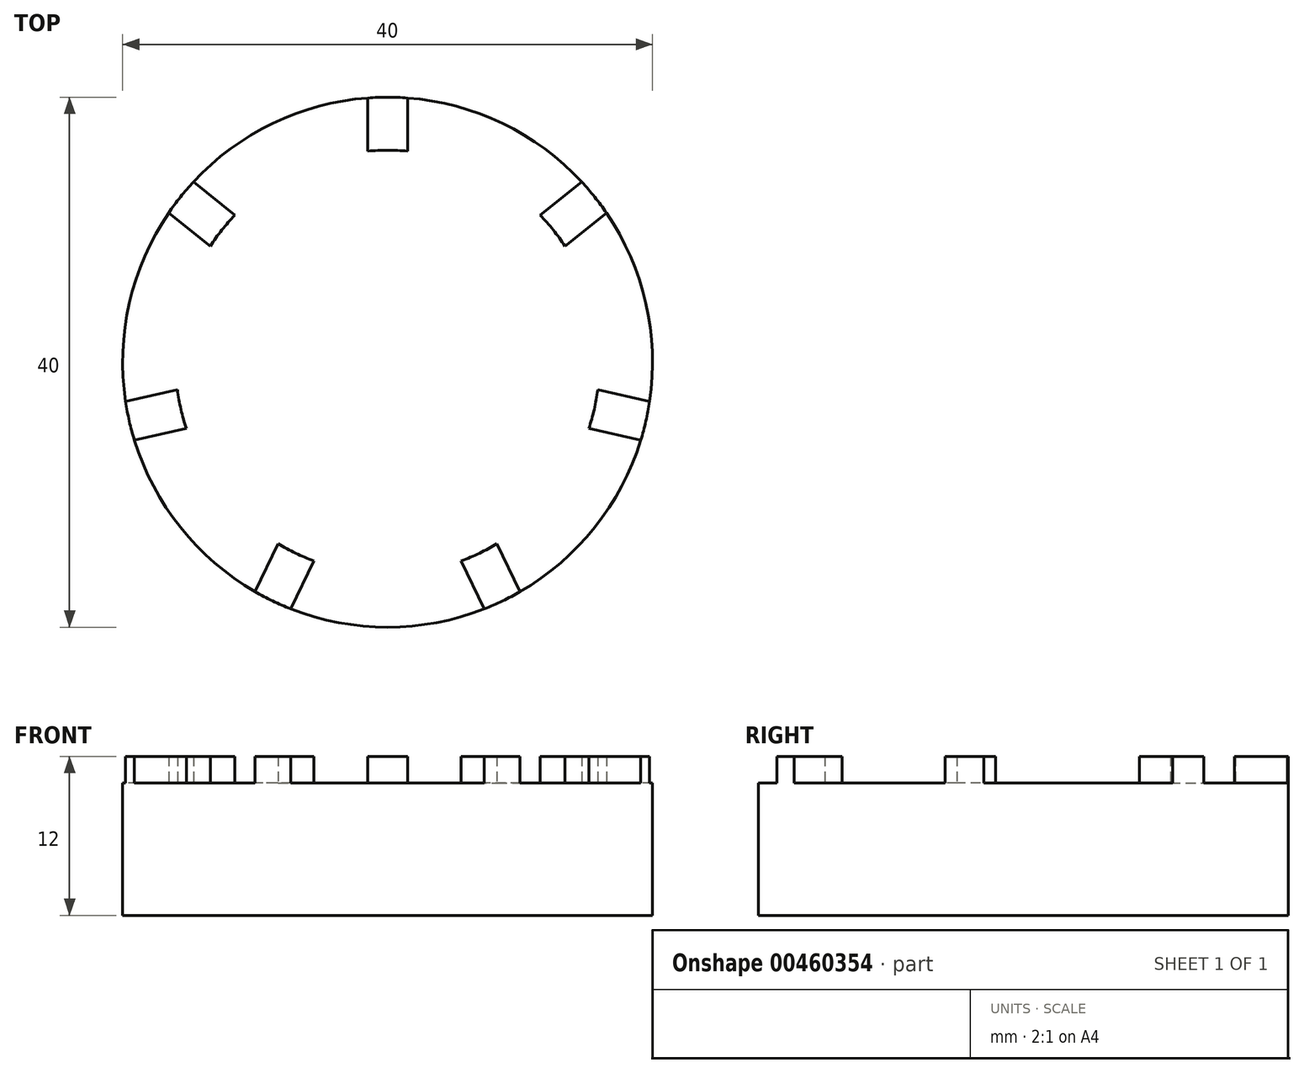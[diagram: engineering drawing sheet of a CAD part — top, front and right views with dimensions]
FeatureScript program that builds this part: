
annotation { "Feature Type Name" : "Feature", "Feature Type Description" : "" }
export const myFeature = defineFeature(function(context is Context, id is Id, definition is map)
    precondition{}
    {
        {
            var Q0;
            Q0=qCreatedBy(makeId("Top.planeOp"),FACE);
            var sketch = newSketch(context, id + "F0", { "sketchPlane" : qUnion([Q0])});
            skCircle(sketch, "E0", {"center": v(0, 0) * mm, "radius": 20 * mm});
            skSolve(sketch);
        }
        {
            var Q0;
            Q0=makeQuery(id+"F0.imprint","IMPRINT",FACE,{"disambiguationData":[TD([[makeQuery(id+"F0.imprint","IMPRINT",EDGE,{"derivedFrom":sQuery(id+"F0.wireOp",EDGE,"E0")}),1.0]])]});
            extrude(context, id + "F1", {"entities" : qUnion([Q0]), "depth" : 10 * mm});
        }
        {
            var Q0;
            Q0=makeQuery(id+"F1.opExtrude","CAP_FACE",FACE,{"disambiguationData":[OSD([sQuery(id+"F0.wireOp",EDGE,"E0")])],"isStart":false});
            var sketch = newSketch(context, id + "F2", { "sketchPlane" : qUnion([Q0])});
            skArc(sketch, "E1.0", {"start": v(1.5, 19.94) * mm, "mid": v(0, 20) * mm, "end": v(-1.5, 19.94) * mm});
            skArc(sketch, "E2", {"start": v(1.5, 15.93) * mm, "mid": v(0, 16) * mm, "end": v(-1.5, 15.93) * mm});
            skLineSegment(sketch, "E3", {"start": v(-1.5, 15.93) * mm, "end": v(-1.5, 19.94) * mm});
            skLineSegment(sketch, "E4", {"start": v(1.5, 15.93) * mm, "end": v(1.5, 19.94) * mm});
            skLineSegment(sketch, "E5", {"start": v(0, 0) * mm, "end": v(0, 16) * mm, "construction": true});
            skSolve(sketch);
        }
        {
            var Q0;
            Q0 = qSketchRegion(id + "F2", true);
            extrude(context, id + "F3", {"entities" : qUnion([Q0]), "operationType" : NewBodyOperationType.ADD, "depth" : 2 * mm});
        }
        {
            var Q0;
            Q0=makeQuery(id+"F1.opExtrude","SWEPT_BODY",BODY,{"disambiguationData":[OSD([sQuery(id+"F0.wireOp",EDGE,"E0")])]});
            var Q1;
            Q1=makeQuery(id+"F3.boolean.opBoolean","MERGE",FACE,{"derivedFrom":[makeQuery(id+"F1.opExtrude","SWEPT_FACE",FACE,{"disambiguationData":[OSD([sQuery(id+"F0.wireOp",EDGE,"E0")])]}),makeQuery(id+"F3.opExtrude","SWEPT_FACE",FACE,{"disambiguationData":[OSD([sQuery(id+"F2.wireOp",EDGE,"E1.0")])]})]});
            circularPattern(context, id + "F4", {"operationType" : NewBodyOperationType.ADD, "entities" : qUnion([Q0]), "axis" : qUnion([Q1]), "angle" : 360 * degree, "instanceCount" : 7, "equalSpace" : true});
        }
    });
